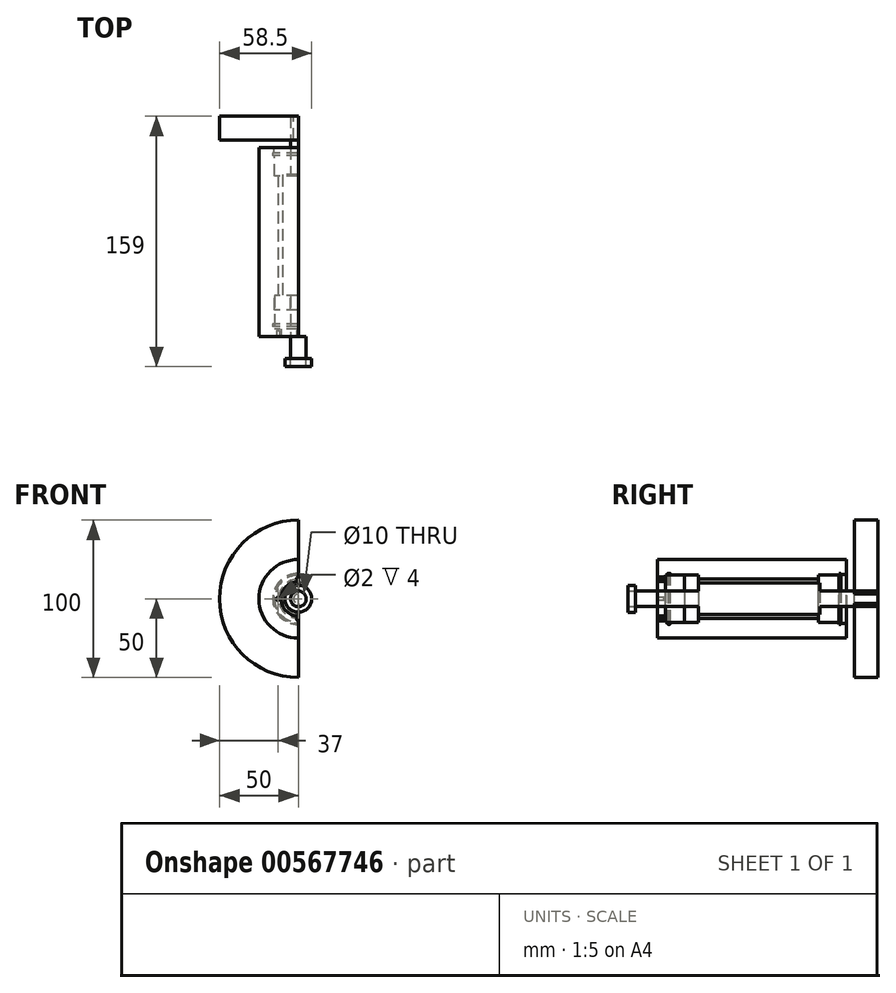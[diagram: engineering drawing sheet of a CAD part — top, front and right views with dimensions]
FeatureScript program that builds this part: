
annotation { "Feature Type Name" : "Feature", "Feature Type Description" : "" }
export const myFeature = defineFeature(function(context is Context, id is Id, definition is map)
    precondition{}
    {
        {
            var Q0;
            Q0=qCreatedBy(makeId("Front.planeOp"),FACE);
            var sketch = newSketch(context, id + "F0", { "sketchPlane" : qUnion([Q0])});
            skCircle(sketch, "E0", {"center": v(0, 0) * mm, "radius": 25 * mm});
            skCircle(sketch, "E1", {"center": v(0, 0) * mm, "radius": 12.5 * mm});
            skSolve(sketch);
        }
        {
            var Q0;
            Q0 = qSketchRegion(id + "F0", true);
            extrude(context, id + "F1", {"entities" : qUnion([Q0]), "depth" : 120 * mm, "offsetDistance" : 25 * mm});
        }
        {
            var Q0;
            Q0=makeQuery(id+"F1.opExtrude","CAP_FACE",FACE,{"disambiguationData":[OSD([sQuery(id+"F0.wireOp",EDGE,"E0"),sQuery(id+"F0.wireOp",EDGE,"E1")])],"isStart":false});
            var sketch = newSketch(context, id + "F2", { "sketchPlane" : qUnion([Q0])});
            skCircle(sketch, "E2", {"center": v(0, 0) * mm, "radius": 15 * mm});
            skSolve(sketch);
        }
        {
            var Q0;
            Q0 = qSketchRegion(id + "F2", true);
            extrude(context, id + "F3", {"entities" : qUnion([Q0]), "operationType" : NewBodyOperationType.REMOVE, "oppositeDirection" : true, "depth" : 26 * mm, "offsetDistance" : 25 * mm});
        }
        {
            var Q0;
            Q0=makeQuery(id+"F1.opExtrude","CAP_FACE",FACE,{"disambiguationData":[OSD([sQuery(id+"F0.wireOp",EDGE,"E0"),sQuery(id+"F0.wireOp",EDGE,"E1")])],"isStart":true});
            var sketch = newSketch(context, id + "F4", { "sketchPlane" : qUnion([Q0])});
            skCircle(sketch, "E3", {"center": v(0, 0) * mm, "radius": 15 * mm});
            skSolve(sketch);
        }
        {
            var Q0;
            Q0 = qSketchRegion(id + "F4", true);
            extrude(context, id + "F5", {"entities" : qUnion([Q0]), "operationType" : NewBodyOperationType.REMOVE, "oppositeDirection" : true, "depth" : 18 * mm, "offsetDistance" : 25 * mm});
        }
        {
            var Q0;
            Q0=makeQuery(id+"F3.boolean.opBoolean","COPY",FACE,{"derivedFrom":makeQuery(id+"F3.opExtrude","CAP_FACE",FACE,{"disambiguationData":[OSD([sQuery(id+"F2.wireOp",EDGE,"E2")])],"isStart":false})});
            var sketch = newSketch(context, id + "F6", { "sketchPlane" : qUnion([Q0])});
            skCircle(sketch, "E4", {"center": v(0, 0) * mm, "radius": 15 * mm});
            skCircle(sketch, "E5", {"center": v(0, 0) * mm, "radius": 5 * mm});
            skSolve(sketch);
        }
        {
            var Q0;
            Q0 = qSketchRegion(id + "F6", true);
            extrude(context, id + "F7", {"entities" : qUnion([Q0]), "depth" : 9 * mm, "offsetDistance" : 25 * mm});
        }
        {
            var Q0;
            Q0=makeQuery(id+"F1.opExtrude","CAP_FACE",FACE,{"disambiguationData":[OSD([sQuery(id+"F0.wireOp",EDGE,"E0"),sQuery(id+"F0.wireOp",EDGE,"E1")])],"isStart":true});
            var sketch = newSketch(context, id + "F8", { "sketchPlane" : qUnion([Q0])});
            skCircle(sketch, "E6", {"center": v(0, 0) * mm, "radius": 15.5 * mm});
            skSolve(sketch);
        }
        {
            var Q0;
            Q0 = qSketchRegion(id + "F8", true);
            extrude(context, id + "F9", {"entities" : qUnion([Q0]), "operationType" : NewBodyOperationType.REMOVE, "oppositeDirection" : true, "depth" : 5 * mm, "offsetDistance" : 25 * mm});
        }
        {
            var Q0;
            Q0=qCreatedBy(makeId("Top.planeOp"),FACE);
            var sketch = newSketch(context, id + "F10", { "sketchPlane" : qUnion([Q0])});
            skLineSegment(sketch, "E7.bottom", {"start": v(14.22, -3.5) * mm, "end": v(16.25, -3.5) * mm});
            skLineSegment(sketch, "E7.top", {"start": v(14.22, -5) * mm, "end": v(16.25, -5) * mm});
            skLineSegment(sketch, "E7.left", {"start": v(14.22, -3.5) * mm, "end": v(14.22, -5) * mm});
            skLineSegment(sketch, "E7.right", {"start": v(16.25, -3.5) * mm, "end": v(16.25, -5) * mm});
            skLineSegment(sketch, "E8", {"start": v(0, 0) * mm, "end": v(0, -8.53) * mm});
            skSolve(sketch);
        }
        {
            var Q0;
            Q0 = qSketchRegion(id + "F10", true);
            var Q1;
            Q1=sQuery(id+"F10.wireOp",EDGE,"E8");
            revolve(context, id + "F11", {"operationType" : NewBodyOperationType.REMOVE, "entities" : qUnion([Q0]), "axis" : qUnion([Q1]), "revolveType" : RevolveType.FULL, "oppositeDirection" : true});
        }
        {
            var Q0;
            Q0=makeQuery(id+"F1.opExtrude","CAP_FACE",FACE,{"disambiguationData":[OSD([sQuery(id+"F0.wireOp",EDGE,"E0"),sQuery(id+"F0.wireOp",EDGE,"E1")])],"isStart":false});
            var sketch = newSketch(context, id + "F12", { "sketchPlane" : qUnion([Q0])});
            skCircle(sketch, "E9", {"center": v(0, 0) * mm, "radius": 15.5 * mm});
            skSolve(sketch);
        }
        {
            var Q0;
            Q0 = qSketchRegion(id + "F12", true);
            extrude(context, id + "F13", {"entities" : qUnion([Q0]), "operationType" : NewBodyOperationType.REMOVE, "oppositeDirection" : true, "depth" : 8 * mm, "offsetDistance" : 25 * mm});
        }
        {
            var Q0;
            Q0=qCreatedBy(makeId("Right.planeOp"),FACE);
            var sketch = newSketch(context, id + "F14", { "sketchPlane" : qUnion([Q0])});
            skLineSegment(sketch, "E10.bottom", {"start": v(-112, 12.85) * mm, "end": v(-113.5, 12.85) * mm});
            skLineSegment(sketch, "E10.top", {"start": v(-112, 16.25) * mm, "end": v(-113.5, 16.25) * mm});
            skLineSegment(sketch, "E10.left", {"start": v(-112, 12.85) * mm, "end": v(-112, 16.25) * mm});
            skLineSegment(sketch, "E10.right", {"start": v(-113.5, 12.85) * mm, "end": v(-113.5, 16.25) * mm});
            skLineSegment(sketch, "E11", {"start": v(0, 0) * mm, "end": v(-186, 0) * mm});
            skSolve(sketch);
        }
        {
            var Q0;
            Q0 = qSketchRegion(id + "F14", true);
            var Q1;
            Q1=sQuery(id+"F14.wireOp",EDGE,"E11");
            revolve(context, id + "F15", {"operationType" : NewBodyOperationType.REMOVE, "entities" : qUnion([Q0]), "axis" : qUnion([Q1]), "revolveType" : RevolveType.FULL, "oppositeDirection" : true});
        }
        {
            var Q0;
            Q0=makeQuery(id+"F1.opExtrude","CAP_FACE",FACE,{"disambiguationData":[OSD([sQuery(id+"F0.wireOp",EDGE,"E0"),sQuery(id+"F0.wireOp",EDGE,"E1")])],"isStart":false});
            var sketch = newSketch(context, id + "F16", { "sketchPlane" : qUnion([Q0])});
            skCircle(sketch, "E12", {"center": v(0, 0) * mm, "radius": 11 * mm});
            skCircle(sketch, "E13", {"center": v(0, 0) * mm, "radius": 16 * mm});
            skSolve(sketch);
        }
        {
            var Q0;
            Q0 = qSketchRegion(id + "F16", true);
            extrude(context, id + "F17", {"entities" : qUnion([Q0]), "oppositeDirection" : true, "depth" : 5 * mm, "offsetDistance" : 25 * mm});
        }
        {
            var Q0;
            Q0=makeQuery(id+"F17.opExtrude","CAP_FACE",FACE,{"disambiguationData":[OSD([sQuery(id+"F16.wireOp",EDGE,"E12"),sQuery(id+"F16.wireOp",EDGE,"E13")])],"isStart":true});
            var sketch = newSketch(context, id + "F18", { "sketchPlane" : qUnion([Q0])});
            skCircle(sketch, "E14", {"center": v(0, 13) * mm, "radius": 1 * mm});
            skCircle(sketch, "E15", {"center": v(0, -13) * mm, "radius": 1 * mm});
            skCircle(sketch, "E16", {"center": v(-13, 0) * mm, "radius": 1 * mm});
            skCircle(sketch, "E17", {"center": v(13, 0) * mm, "radius": 1 * mm});
            skSolve(sketch);
        }
        {
            var Q0;
            Q0 = qSketchRegion(id + "F18", true);
            extrude(context, id + "F19", {"entities" : qUnion([Q0]), "operationType" : NewBodyOperationType.REMOVE, "oppositeDirection" : true, "depth" : 4 * mm, "offsetDistance" : 25 * mm});
        }
        {
            var Q0;
            Q0=makeQuery(id+"F17.opExtrude","CAP_FACE",FACE,{"disambiguationData":[OSD([sQuery(id+"F16.wireOp",EDGE,"E12"),sQuery(id+"F16.wireOp",EDGE,"E13")])],"isStart":false});
            var sketch = newSketch(context, id + "F20", { "sketchPlane" : qUnion([Q0])});
            skCircle(sketch, "E18", {"center": v(0, 0) * mm, "radius": 15 * mm});
            skCircle(sketch, "E19.0", {"center": v(0, 0) * mm, "radius": 16 * mm});
            skSolve(sketch);
        }
        {
            var Q0;
            Q0 = qSketchRegion(id + "F20", true);
            extrude(context, id + "F21", {"entities" : qUnion([Q0]), "operationType" : NewBodyOperationType.ADD, "depth" : 3 * mm, "offsetDistance" : 25 * mm});
        }
        {
            var Q0;
            Q0=qCreatedBy(makeId("Top.planeOp"),FACE);
            var sketch = newSketch(context, id + "F22", { "sketchPlane" : qUnion([Q0])});
            skLineSegment(sketch, "E20", {"start": v(0, 0) * mm, "end": v(0, 49.6) * mm});
            skLineSegment(sketch, "E21", {"start": v(5, -134) * mm, "end": v(5, -94) * mm});
            skLineSegment(sketch, "E22", {"start": v(5, -94) * mm, "end": v(10, -94) * mm});
            skLineSegment(sketch, "E23", {"start": v(10, -94) * mm, "end": v(10, -17) * mm});
            skLineSegment(sketch, "E24", {"start": v(10, -17) * mm, "end": v(5, -17) * mm});
            skLineSegment(sketch, "E25", {"start": v(5, -17) * mm, "end": v(5, 20) * mm});
            skLineSegment(sketch, "E26", {"start": v(5, 20) * mm, "end": v(0, 20) * mm});
            skLineSegment(sketch, "E27", {"start": v(0, 20) * mm, "end": v(0, -134) * mm});
            skLineSegment(sketch, "E28", {"start": v(0, -134) * mm, "end": v(5, -134) * mm});
            skSolve(sketch);
        }
        {
            var Q0;
            Q0 = qSketchRegion(id + "F22", true);
            var Q1;
            Q1=sQuery(id+"F22.wireOp",EDGE,"E20");
            revolve(context, id + "F23", {"entities" : qUnion([Q0]), "axis" : qUnion([Q1]), "revolveType" : RevolveType.FULL});
        }
        {
            var Q0;
            Q0=makeQuery(id+"F23.opRevolve","SWEPT_FACE",FACE,{"disambiguationData":[OSD([sQuery(id+"F22.wireOp",EDGE,"E26")])]});
            var sketch = newSketch(context, id + "F24", { "sketchPlane" : qUnion([Q0])});
            skCircle(sketch, "E29", {"center": v(0, 0) * mm, "radius": 50 * mm});
            skCircle(sketch, "E30", {"center": v(0, 0) * mm, "radius": 3 * mm});
            skSolve(sketch);
        }
        {
            var Q0;
            Q0 = qSketchRegion(id + "F24", true);
            extrude(context, id + "F25", {"entities" : qUnion([Q0]), "oppositeDirection" : true, "depth" : 15 * mm, "offsetDistance" : 25 * mm});
        }
        {
            var Q0;
            Q0=makeQuery(id+"F23.opRevolve","SWEPT_FACE",FACE,{"disambiguationData":[OSD([sQuery(id+"F22.wireOp",EDGE,"E28")])]});
            var sketch = newSketch(context, id + "F26", { "sketchPlane" : qUnion([Q0])});
            skCircle(sketch, "E31", {"center": v(0, 0) * mm, "radius": 4.5 * mm});
            skCircle(sketch, "E32", {"center": v(0, 0) * mm, "radius": 8.5 * mm});
            skSolve(sketch);
        }
        {
            var Q0;
            Q0=makeQuery(id+"F26.imprint","IMPRINT",FACE,{"disambiguationData":[TD([[makeQuery(id+"F26.imprint","IMPRINT",EDGE,{"derivedFrom":sQuery(id+"F26.wireOp",EDGE,"E32")}),1.0]])]});
            extrude(context, id + "F27", {"entities" : qUnion([Q0]), "depth" : 5 * mm, "offsetDistance" : 25 * mm});
        }
        {
            var Q0;
            Q0=makeQuery(id+"F25.opExtrude","CAP_FACE",FACE,{"disambiguationData":[OSD([sQuery(id+"F24.wireOp",EDGE,"E29"),sQuery(id+"F24.wireOp",EDGE,"E30")])],"isStart":false});
            var sketch = newSketch(context, id + "F28", { "sketchPlane" : qUnion([Q0])});
            skLineSegment(sketch, "E33.bottom", {"start": v(0, 66.82) * mm, "end": v(119.8, 66.82) * mm});
            skLineSegment(sketch, "E33.top", {"start": v(0, -74.28) * mm, "end": v(119.8, -74.28) * mm});
            skLineSegment(sketch, "E33.left", {"start": v(0, 66.82) * mm, "end": v(0, -74.28) * mm});
            skLineSegment(sketch, "E33.right", {"start": v(119.8, 66.82) * mm, "end": v(119.8, -74.28) * mm});
            skSolve(sketch);
        }
        {
            var Q0;
            {var subQ0=sQuery(id+"F28.wireOp",EDGE,"E33.left");var subQ1=makeQuery(id+"F25.opExtrude","CAP_EDGE",EDGE,{"disambiguationData":[OSD([sQuery(id+"F24.wireOp",EDGE,"E29")])],"isStart":false});var subQ2=makeQuery(id+"F28.imprint","INTERSECT",VERTEX,{"disambiguationData":[OD(0.0)],"derivedFrom":[subQ1,subQ0]});Q0=makeQuery(id+"F28.imprint","IMPRINT",FACE,{"disambiguationData":[TD([[makeQuery(id+"F28.imprint","IMPRINT",EDGE,{"disambiguationData":[TD([[subQ2,-1.0]])],"derivedFrom":subQ0}),1.0]])]});}
            extrude(context, id + "F29", {"entities" : qUnion([Q0]), "operationType" : NewBodyOperationType.REMOVE, "oppositeDirection" : true, "depth" : 25 * mm, "offsetDistance" : 25 * mm});
        }
        {
            var Q0;
            Q0=makeQuery(id+"F1.opExtrude","CAP_FACE",FACE,{"disambiguationData":[OSD([sQuery(id+"F0.wireOp",EDGE,"E0"),sQuery(id+"F0.wireOp",EDGE,"E1")])],"isStart":false});
            var sketch = newSketch(context, id + "F30", { "sketchPlane" : qUnion([Q0])});
            skLineSegment(sketch, "E34.bottom", {"start": v(0, -63.8) * mm, "end": v(78.12, -63.8) * mm});
            skLineSegment(sketch, "E34.top", {"start": v(0, 54.1) * mm, "end": v(78.12, 54.1) * mm});
            skLineSegment(sketch, "E34.left", {"start": v(0, -63.8) * mm, "end": v(0, 54.1) * mm});
            skLineSegment(sketch, "E34.right", {"start": v(78.12, -63.8) * mm, "end": v(78.12, 54.1) * mm});
            skSolve(sketch);
        }
        {
            var Q0;
            Q0 = qSketchRegion(id + "F30", true);
            extrude(context, id + "F31", {"entities" : qUnion([Q0]), "operationType" : NewBodyOperationType.REMOVE, "oppositeDirection" : true, "depth" : 148.1 * mm, "offsetDistance" : 25 * mm});
        }
    });
